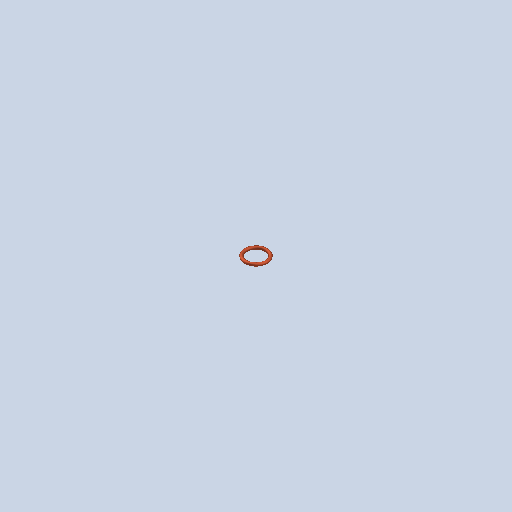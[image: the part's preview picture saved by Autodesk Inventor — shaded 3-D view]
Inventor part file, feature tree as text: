
AUTODESK INVENTOR PART (.ipt)
format: ipt  version: 2024 (Build 280153000, 153)  size: 89,088 bytes
history: native  units: in
note: dims shown in document units (in); Inventor stores cm internally (conversion verified against a paired STEP export)
features: revolve x1, direct_edit x1, sketch x1, other x1
ambient origin geometry x8: Origin, YZ Plane, XZ Plane, XY Plane, X Axis, Y Axis, Z Axis, Center Point
bodies: Solid1 (feature_tree)
feature tree (4):
  revolve  "Revolution1"  [1 undecoded]
  direct_edit  "Direct Edit1"
  sketch  "Sketch1"  dims[d0=0.2117in d1=0.0625in d2=90.0deg d3=3.937in d4=0.3937in d5=0.3937in]
  other  "Scale1"
note: 1 required parameter value undecoded (feature->parameter linkage not recoverable at this tier; creation-order binding heuristic only, values carry confidence <= 0.55)
